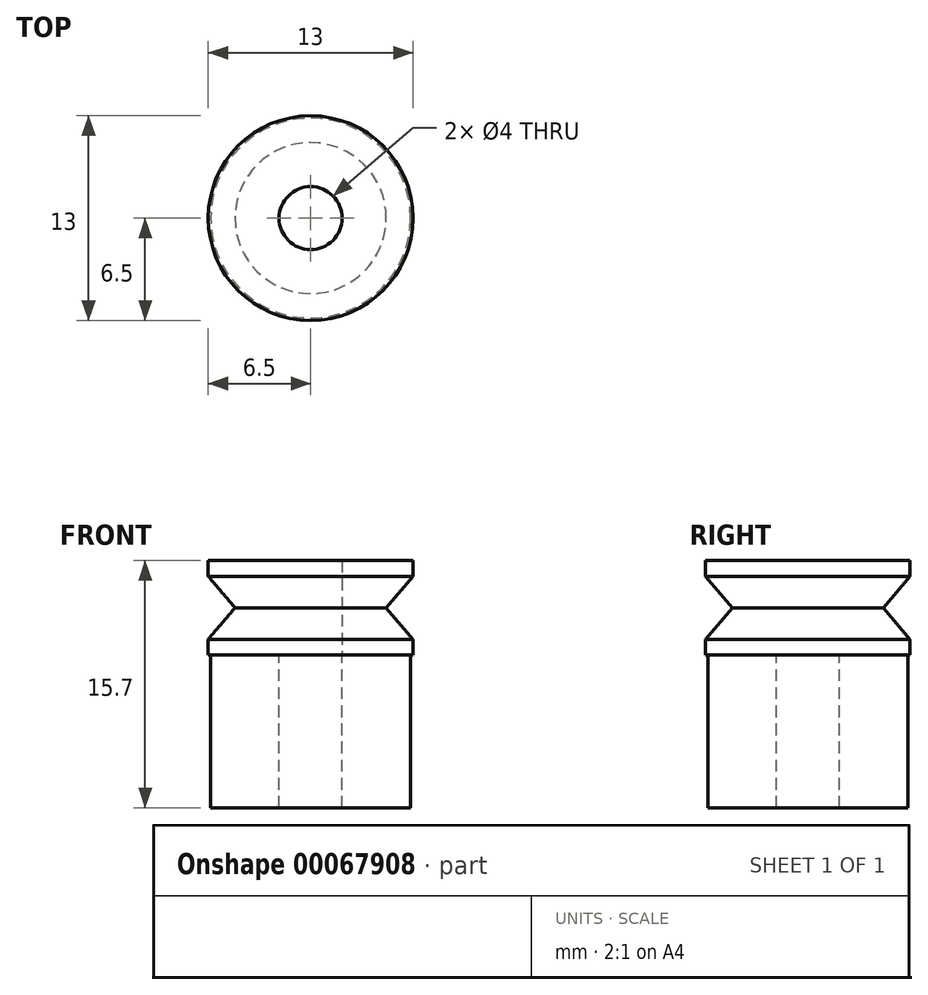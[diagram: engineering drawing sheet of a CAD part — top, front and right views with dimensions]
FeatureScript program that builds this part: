
annotation { "Feature Type Name" : "Feature", "Feature Type Description" : "" }
export const myFeature = defineFeature(function(context is Context, id is Id, definition is map)
    precondition{}
    {
        {
            var Q0;
            Q0=qCreatedBy(makeId("Top.planeOp"),FACE);
            var sketch = newSketch(context, id + "F0", { "sketchPlane" : qUnion([Q0])});
            skCircle(sketch, "E0", {"center": v(0, 0) * mm, "radius": 2 * mm});
            skCircle(sketch, "E1", {"center": v(0, 0) * mm, "radius": 6.5 * mm});
            skSolve(sketch);
        }
        {
            var Q0;
            Q0=makeQuery(id+"F0.imprint","IMPRINT",FACE,{"disambiguationData":[TD([[makeQuery(id+"F0.imprint","IMPRINT",EDGE,{"derivedFrom":sQuery(id+"F0.wireOp",EDGE,"E0")}),-1.0]])]});
            extrude(context, id + "F1", {"entities" : qUnion([Q0]), "depth" : 6 * mm});
        }
        {
            var Q0;
            Q0=qCreatedBy(makeId("Front.planeOp"),FACE);
            var sketch = newSketch(context, id + "F2", { "sketchPlane" : qUnion([Q0])});
            skLineSegment(sketch, "E2", {"start": v(6.5, 5) * mm, "end": v(4.8, 3) * mm});
            skLineSegment(sketch, "E3", {"start": v(6.5, 1) * mm, "end": v(4.8, 3) * mm});
            skLineSegment(sketch, "E4", {"start": v(6.5, 5) * mm, "end": v(6.5, 1) * mm});
            skSolve(sketch);
        }
        {
            var Q0;
            Q0=makeQuery(id+"F2.imprint","IMPRINT",FACE,{"disambiguationData":[TD([[makeQuery(id+"F2.imprint","IMPRINT",EDGE,{"derivedFrom":sQuery(id+"F2.wireOp",EDGE,"E2")}),1.0]])]});
            var Q1;
            Q1=makeQuery(id+"F1.opExtrude","SWEPT_FACE",FACE,{"disambiguationData":[OSD([sQuery(id+"F0.wireOp",EDGE,"E1")])]});
            revolve(context, id + "F3", {"operationType" : NewBodyOperationType.REMOVE, "entities" : qUnion([Q0]), "axis" : qUnion([Q1]), "revolveType" : RevolveType.FULL, "oppositeDirection" : true});
        }
        {
            var Q0;
            Q0=qCreatedBy(makeId("Top.planeOp"),FACE);
            var sketch = newSketch(context, id + "F4", { "sketchPlane" : qUnion([Q0])});
            skCircle(sketch, "E5", {"center": v(0, 0) * mm, "radius": 6.35 * mm});
            skCircle(sketch, "E6", {"center": v(0, 0) * mm, "radius": 2 * mm});
            skSolve(sketch);
        }
        {
            var Q0;
            Q0=makeQuery(id+"F4.imprint","IMPRINT",FACE,{"disambiguationData":[TD([[makeQuery(id+"F4.imprint","IMPRINT",EDGE,{"derivedFrom":sQuery(id+"F4.wireOp",EDGE,"E5")}),1.0]])]});
            extrude(context, id + "F5", {"entities" : qUnion([Q0]), "oppositeDirection" : true, "depth" : 9.7 * mm});
        }
    });
